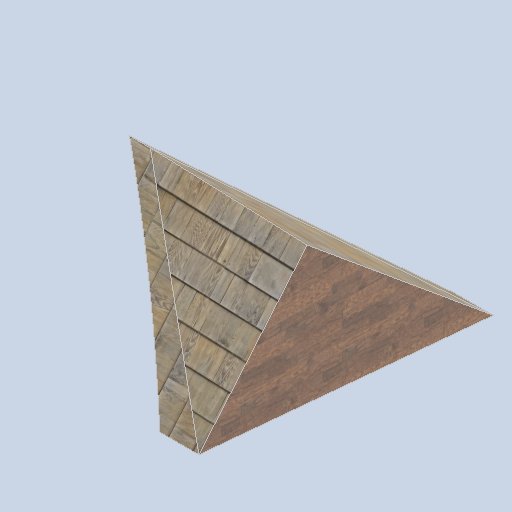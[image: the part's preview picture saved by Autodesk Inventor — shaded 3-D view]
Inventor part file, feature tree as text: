
AUTODESK INVENTOR PART (.ipt)
format: ipt  version: 2024.2 (Build 282272000, 272)  size: 239,104 bytes
history: native  units: in
note: dims shown in document units (in); Inventor stores cm internally (conversion verified against a paired STEP export)
features: sketch x6, plane x5, other x3
ambient origin geometry x8: Origin, YZ Plane, XZ Plane, XY Plane, X Axis, Y Axis, Z Axis, Center Point
bodies: Solid1 (feature_tree)
feature tree (14):
  other  "panel_pad_03.ipt"
  other  "Solid1::panel_pad_03.ipt"
  other  "TaggingFeature1"
  sketch  "Sketch1"  dims[d0=0.3937in]
  sketch  "Sketch2"
  sketch  "Sketch3"
  sketch  "Sketch6"
  sketch  "Sketch7"
  sketch  "Sketch8"
  plane  "Work Plane1"
  plane  "Work Plane2"
  plane  "Work Plane3"
  plane  "Work Plane4"
  plane  "Work Plane5"
